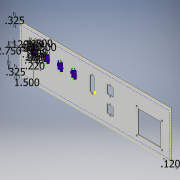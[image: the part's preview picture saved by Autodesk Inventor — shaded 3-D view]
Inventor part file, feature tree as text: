
AUTODESK INVENTOR PART (.ipt)
format: ipt  version: 2017 (Build 210142000, 142)  size: 294,400 bytes
history: native  units: in
note: dims shown in document units (in); Inventor stores cm internally (conversion verified against a paired STEP export)
features: extrude x5, hole x4, other x3, sketch x3
ambient origin geometry x8: Origin, YZ Plane, XZ Plane, XY Plane, X Axis, Y Axis, Z Axis, Center Point
bodies: Solid1 (feature_tree)
feature tree (15):
  extrude  "pdu"  Depth=5.256in
  other  "dsub9 sketch"
  other  "dsub25 sketch"
  other  "CAT7 sketch"
  hole  "airflow holes"  [1 undecoded]
  extrude  "airflow cutout"  Depth=0.3937in
  hole  "dsub9 4-40 holes"  [1 undecoded]
  hole  "CAT7 holes"  [1 undecoded]
  extrude  "CAT7 cutout"  Depth=0.3937in
  hole  "dsub25 4-40 holes"  [1 undecoded]
  extrude  "dsub25 cutout"  Depth=1.5in
  extrude  "Extrusion10"  Depth=0.3937in
  sketch  "Sketch1"  dims[d0=16.73in d1=5.256in]
  sketch  "Sketch5"  dims[d2=0.065in d3=0.0in d4=0.089in]
  sketch  "Sketch7"  dims[d5=0.089in d6=0.984in d13=0.325in d14=0.325in d15=0.12in d16=0.12in d17=1.5in d20=2.75in d24=1.5in d31=0.089in d32=0.089in d33=1.852in d34=0.166in d35=0.166in d36=0.166in d37=0.166in d38=1.452in d39=1.577in d40=2.0in d41=0.44in d42=0.22in d43=8.0in d44=2.319in d47=0.9in d48=0.675in d49=0.089in d50=0.089in d51=1.142in d52=3.029in d53=10.0in d54=0.7874in d56=1.852in d57=0.3937in d59=1.0in d63=3.3in d64=3.3in d65=12.7in d66=0.535in d67=2.5in d68=2.5in d69=2.81in d70=0.177in d71=0.177in d72=0.177in d73=0.177in d76=0.177in d77=0.75in d78=0.332in d79=0.25in d80=0.5635in d81=1.0in d82=0.8108in d83=3.3in d84=3.3in d85=12.7in d86=0.535in d87=2.5in d88=2.5in d89=2.81in d90=0.177in d91=0.177in d92=0.177in d93=0.177in d94=0.0in d95=0.0in d96=0.085in d97=0.224in d98=0.375in d99=0.25in d100=0.5635in d101=0.349in d102=0.8108in d105=0.116in d106=0.224in d107=0.375in d108=0.25in d109=0.5635in d110=0.349in d111=0.8108in d112=0.0in d113=0.0in d114=0.085in d115=0.224in d116=0.375in d117=0.25in d118=0.5635in d119=0.349in d120=0.8108in d121=0.0in d122=0.0in d123=0.166in d124=0.166in d125=0.166in d126=0.166in d127=0.44in d128=0.708in d129=0.583in d130=0.22in d131=1.5748in d133=1.5in d134=0.3937in d136=1.0in d138=1.0in d139=0.0in]
note: 4 required parameter values undecoded (feature->parameter linkage not recoverable at this tier; creation-order binding heuristic only, values carry confidence <= 0.55)
